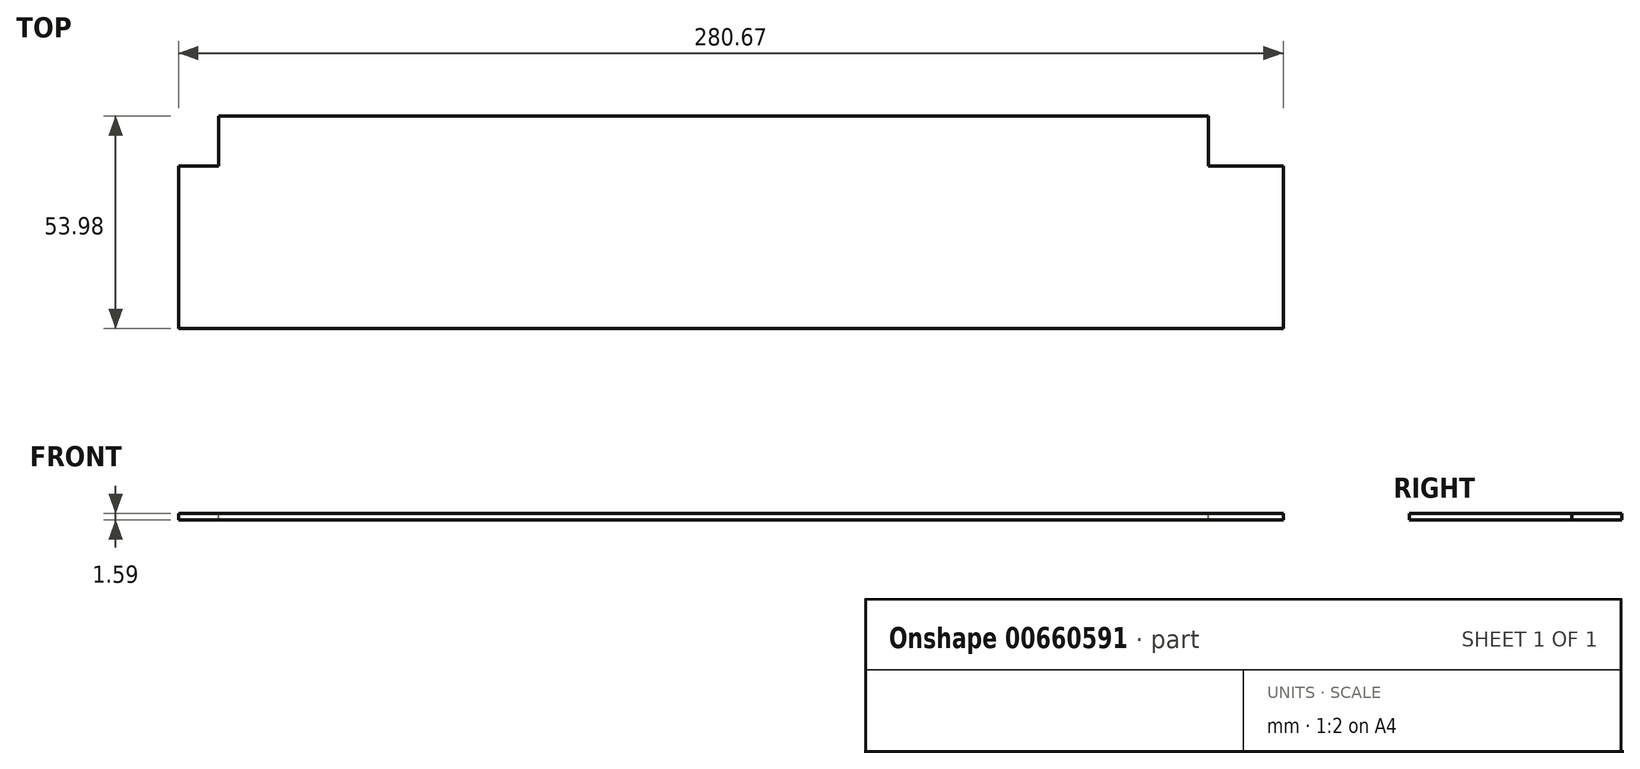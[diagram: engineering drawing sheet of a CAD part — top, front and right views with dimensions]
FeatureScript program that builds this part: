
annotation { "Feature Type Name" : "Feature", "Feature Type Description" : "" }
export const myFeature = defineFeature(function(context is Context, id is Id, definition is map)
    precondition{}
    {
        {
            var Q0;
            Q0=qCreatedBy(makeId("Right.planeOp"),FACE);
            var sketch = newSketch(context, id + "F0", { "sketchPlane" : qUnion([Q0])});
            skLineSegment(sketch, "E0", {"start": v(0, 0) * mm, "end": v(-53.98, 0) * mm});
            skLineSegment(sketch, "E1", {"start": v(-53.98, 0) * mm, "end": v(-53.98, 1.59) * mm});
            skLineSegment(sketch, "E2", {"start": v(-53.98, 1.59) * mm, "end": v(0, 1.59) * mm});
            skLineSegment(sketch, "E3", {"start": v(0, 1.59) * mm, "end": v(0, 0) * mm});
            skSolve(sketch);
        }
        {
            var Q0;
            Q0 = qSketchRegion(id + "F0", true);
            extrude(context, id + "F1", {"entities" : qUnion([Q0]), "depth" : 280.67 * mm, "offsetDistance" : 25.4 * mm});
        }
        {
            var Q0;
            Q0=makeQuery(id+"F1.opExtrude","SWEPT_FACE",FACE,{"disambiguationData":[OSD([sQuery(id+"F0.wireOp",EDGE,"E2")])]});
            var sketch = newSketch(context, id + "F2", { "sketchPlane" : qUnion([Q0])});
            skLineSegment(sketch, "E4.bottom", {"start": v(0, 0) * mm, "end": v(10.16, 0) * mm});
            skLineSegment(sketch, "E4.top", {"start": v(0, -12.7) * mm, "end": v(10.16, -12.7) * mm});
            skLineSegment(sketch, "E4.left", {"start": v(0, 0) * mm, "end": v(0, -12.7) * mm});
            skLineSegment(sketch, "E4.right", {"start": v(10.16, 0) * mm, "end": v(10.16, -12.7) * mm});
            skLineSegment(sketch, "E5.bottom", {"start": v(280.67, 0) * mm, "end": v(261.62, 0) * mm});
            skLineSegment(sketch, "E5.top", {"start": v(280.67, -12.7) * mm, "end": v(261.62, -12.7) * mm});
            skLineSegment(sketch, "E5.left", {"start": v(280.67, 0) * mm, "end": v(280.67, -12.7) * mm});
            skLineSegment(sketch, "E5.right", {"start": v(261.62, 0) * mm, "end": v(261.62, -12.7) * mm});
            skSolve(sketch);
        }
        {
            var Q0;
            Q0=makeQuery(id+"F2.imprint","IMPRINT",FACE,{"disambiguationData":[TD([[makeQuery(id+"F2.imprint","IMPRINT",EDGE,{"derivedFrom":sQuery(id+"F2.wireOp",EDGE,"E4.bottom")}),1.0]])]});
            var Q1;
            Q1=makeQuery(id+"F2.imprint","IMPRINT",FACE,{"disambiguationData":[TD([[makeQuery(id+"F2.imprint","IMPRINT",EDGE,{"derivedFrom":sQuery(id+"F2.wireOp",EDGE,"E5.bottom")}),1.0]])]});
            extrude(context, id + "F3", {"entities" : qUnion([Q0, Q1]), "operationType" : NewBodyOperationType.REMOVE, "oppositeDirection" : true, "depth" : 25.4 * mm, "offsetDistance" : 25.4 * mm});
        }
    });
